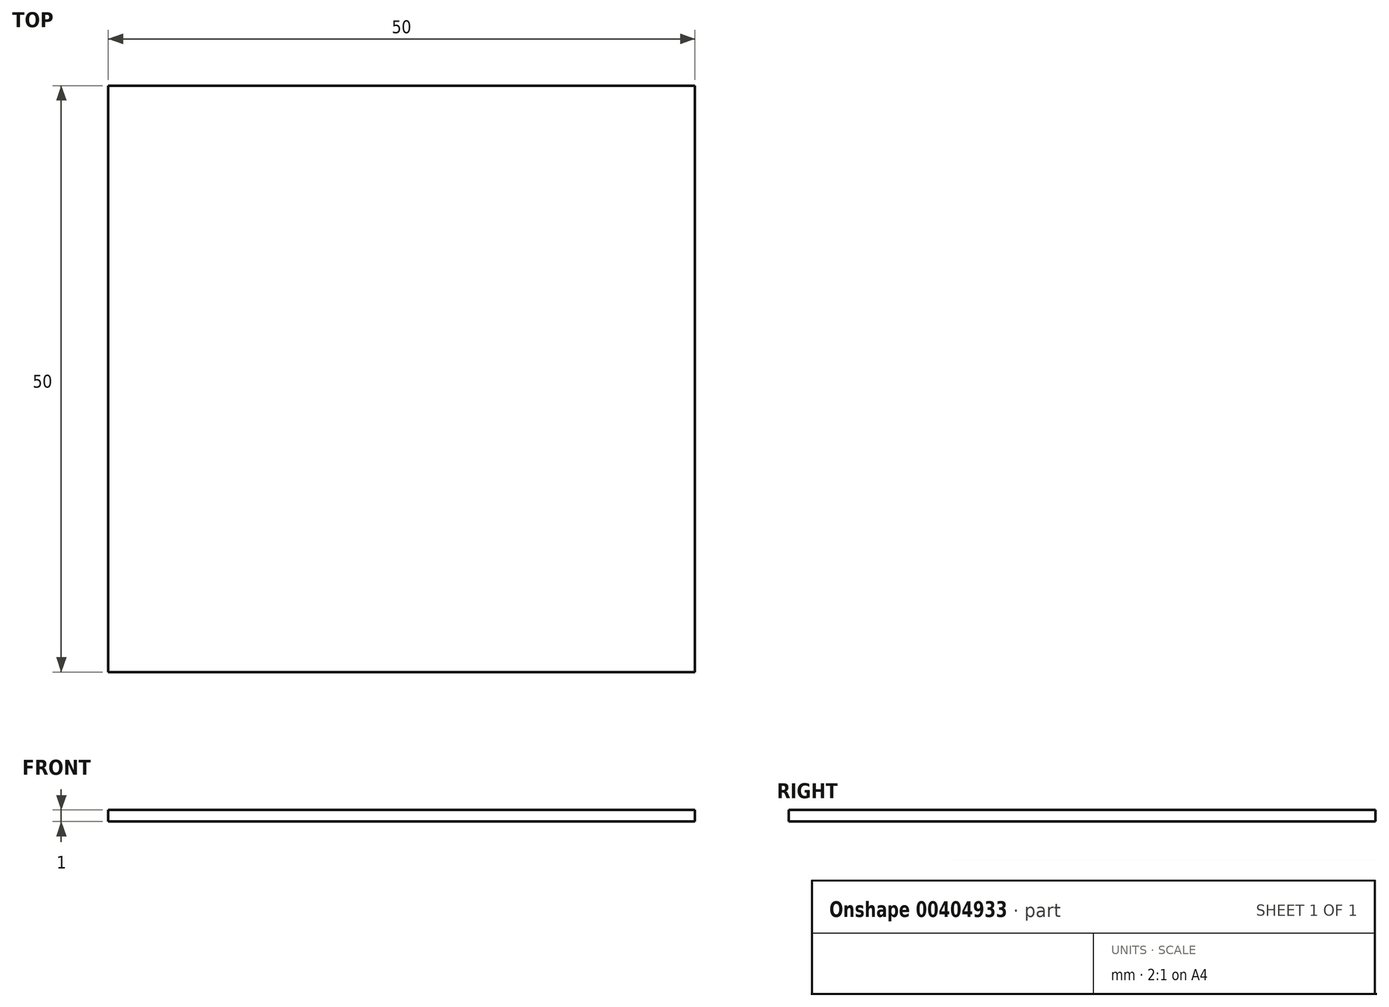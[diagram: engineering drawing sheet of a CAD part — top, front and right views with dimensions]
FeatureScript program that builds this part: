
annotation { "Feature Type Name" : "Feature", "Feature Type Description" : "" }
export const myFeature = defineFeature(function(context is Context, id is Id, definition is map)
    precondition{}
    {
        {
            var Q0;
            Q0=qCreatedBy(makeId("Top.planeOp"),FACE);
            var sketch = newSketch(context, id + "F0", { "sketchPlane" : qUnion([Q0])});
            skLineSegment(sketch, "E0.bottom", {"start": v(-25, -25) * mm, "end": v(25, -25) * mm});
            skLineSegment(sketch, "E0.top", {"start": v(-25, 25) * mm, "end": v(25, 25) * mm});
            skLineSegment(sketch, "E0.left", {"start": v(-25, -25) * mm, "end": v(-25, 25) * mm});
            skLineSegment(sketch, "E0.right", {"start": v(25, -25) * mm, "end": v(25, 25) * mm});
            skSolve(sketch);
        }
        {
            var Q0;
            Q0=makeQuery(id+"F0.imprint","IMPRINT",FACE,{"disambiguationData":[TD([[makeQuery(id+"F0.imprint","IMPRINT",EDGE,{"derivedFrom":sQuery(id+"F0.wireOp",EDGE,"E0.bottom")}),1.0]])]});
            extrude(context, id + "F1", {"entities" : qUnion([Q0]), "depth" : 1 * mm});
        }
    });
